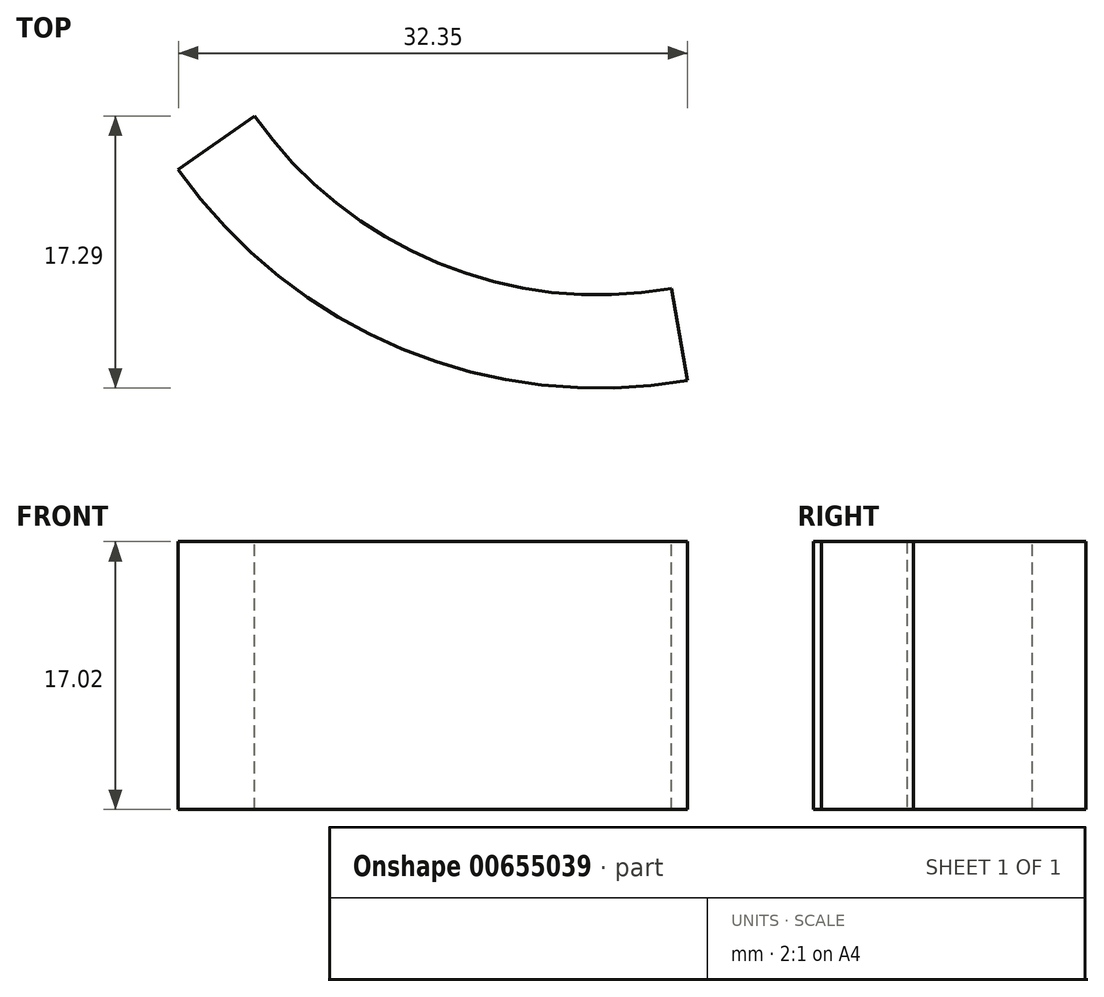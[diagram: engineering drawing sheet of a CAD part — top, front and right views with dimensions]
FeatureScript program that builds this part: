
annotation { "Feature Type Name" : "Feature", "Feature Type Description" : "" }
export const myFeature = defineFeature(function(context is Context, id is Id, definition is map)
    precondition{}
    {
        {
            var Q0;
            Q0=qCreatedBy(makeId("Right.planeOp"),FACE);
            var sketch = newSketch(context, id + "F0", { "sketchPlane" : qUnion([Q0])});
            skLineSegment(sketch, "E0.bottom", {"start": v(-26.67, 0) * mm, "end": v(-32.59, 0) * mm});
            skLineSegment(sketch, "E0.top", {"start": v(-26.67, 17.02) * mm, "end": v(-32.59, 17.02) * mm});
            skLineSegment(sketch, "E0.left", {"start": v(-26.67, 0) * mm, "end": v(-26.67, 17.02) * mm});
            skLineSegment(sketch, "E0.right", {"start": v(-32.59, 0) * mm, "end": v(-32.59, 17.02) * mm});
            skSolve(sketch);
        }
        {
            var Q0;
            Q0=qCreatedBy(makeId("Right.planeOp"),FACE);
            var sketch = newSketch(context, id + "F1", { "sketchPlane" : qUnion([Q0])});
            skLineSegment(sketch, "E1", {"start": v(0, 0) * mm, "end": v(0, 54.44) * mm});
            skSolve(sketch);
        }
        {
            var Q0;
            Q0=qSketchRegion(id+"F0",true);
            var Q1;
            Q1=sQuery(id+"F1.wireOp",EDGE,"E1");
            revolve(context, id + "F2", {"entities" : qUnion([Q0]), "axis" : qUnion([Q1]), "revolveType" : RevolveType.TWO_DIRECTIONS, "angle" : 10 * degree, "angleBack" : 305 * degree});
        }
    });
